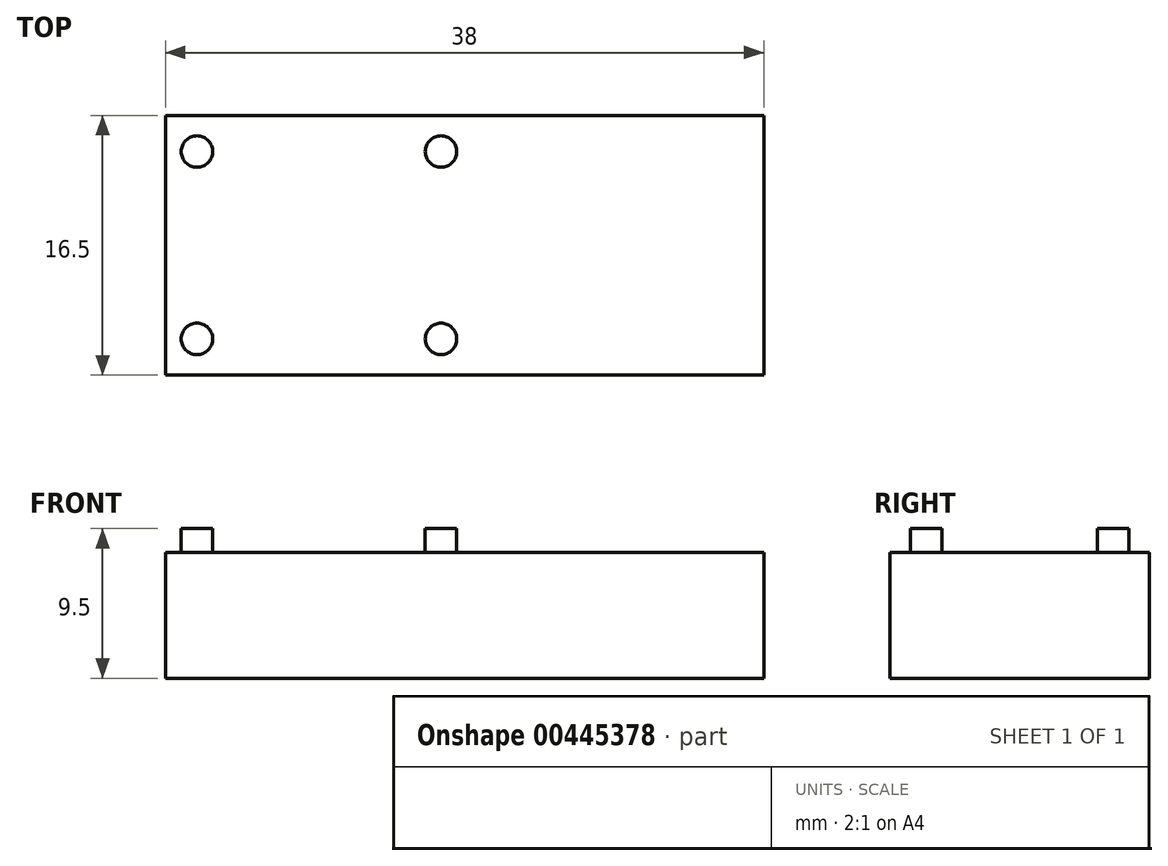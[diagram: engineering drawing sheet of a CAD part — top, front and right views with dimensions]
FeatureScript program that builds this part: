
annotation { "Feature Type Name" : "Feature", "Feature Type Description" : "" }
export const myFeature = defineFeature(function(context is Context, id is Id, definition is map)
    precondition{}
    {
        {
            var Q0;
            Q0=qCreatedBy(makeId("Top.planeOp"),FACE);
            var sketch = newSketch(context, id + "F0", { "sketchPlane" : qUnion([Q0])});
            skLineSegment(sketch, "E0.bottom", {"start": v(-19, 8.25) * mm, "end": v(19, 8.25) * mm});
            skLineSegment(sketch, "E0.top", {"start": v(-19, -8.25) * mm, "end": v(19, -8.25) * mm});
            skLineSegment(sketch, "E0.left", {"start": v(-19, 8.25) * mm, "end": v(-19, -8.25) * mm});
            skLineSegment(sketch, "E0.right", {"start": v(19, 8.25) * mm, "end": v(19, -8.25) * mm});
            skPoint(sketch, "E0.middle", {"position": v(0, 0) * mm});
            skSolve(sketch);
        }
        {
            var Q0;
            Q0=makeQuery(id+"F0.imprint","IMPRINT",FACE,{"disambiguationData":[TD([[makeQuery(id+"F0.imprint","IMPRINT",EDGE,{"derivedFrom":sQuery(id+"F0.wireOp",EDGE,"E0.bottom")}),-1.0]])]});
            extrude(context, id + "F1", {"entities" : qUnion([Q0]), "oppositeDirection" : true, "depth" : 8 * mm});
        }
        {
            var Q0;
            Q0=makeQuery(id+"F1.opExtrude","CAP_FACE",FACE,{"disambiguationData":[OSD([sQuery(id+"F0.wireOp",EDGE,"E0.bottom"),sQuery(id+"F0.wireOp",EDGE,"E0.top"),sQuery(id+"F0.wireOp",EDGE,"E0.left"),sQuery(id+"F0.wireOp",EDGE,"E0.right")])],"isStart":true});
            var sketch = newSketch(context, id + "F2", { "sketchPlane" : qUnion([Q0])});
            skLineSegment(sketch, "E1", {"start": v(-19, 8.25) * mm, "end": v(-17, 8.25) * mm, "construction": true});
            skLineSegment(sketch, "E2", {"start": v(-17, 8.25) * mm, "end": v(-17, -8.25) * mm, "construction": true});
            skLineSegment(sketch, "E3", {"start": v(-19, 0) * mm, "end": v(-17, 0) * mm, "construction": true});
            skLineSegment(sketch, "E4.0", {"start": v(-19, -5.95) * mm, "end": v(-17, -5.95) * mm, "construction": true});
            skLineSegment(sketch, "E5.0", {"start": v(-19, 5.95) * mm, "end": v(-17, 5.95) * mm, "construction": true});
            skCircle(sketch, "E6", {"center": v(-17, 5.95) * mm, "radius": 1 * mm});
            skCircle(sketch, "E7", {"center": v(-17, -5.95) * mm, "radius": 1 * mm});
            skCircle(sketch, "E8.1.0.0", {"center": v(-1.5, 5.95) * mm, "radius": 1 * mm});
            skLineSegment(sketch, "E8.direction1", {"start": v(-17, 5.95) * mm, "end": v(-1.5, 5.95) * mm, "construction": true});
            skCircle(sketch, "E9.1.0.0", {"center": v(-1.5, -5.95) * mm, "radius": 1 * mm});
            skLineSegment(sketch, "E9.direction1", {"start": v(-17, -5.95) * mm, "end": v(-1.5, -5.95) * mm, "construction": true});
            skSolve(sketch);
        }
        {
            var Q0;
            Q0 = qSketchRegion(id + "F2", true);
            extrude(context, id + "F3", {"entities" : qUnion([Q0]), "operationType" : NewBodyOperationType.ADD, "depth" : 1.5 * mm});
        }
    });
